# Revit family: Casual_Space_Division-Teknion-HNBCFG_Navigate_Fixed_Center_Screen_Glass-R2016
name_source: partatom
category: Furniture
revit_build: Autodesk Revit Architecture 2016 (Build: 20190507_1515(x64)
units: mm (PartAtom-declared; Revit-internal decimal feet)

## family parameters
Always vertical = Yes
Cut with Voids When Loaded = No
OmniClass Number = 23.40.20.00
OmniClass Title = General Furniture and Specialties
Room Calculation Point = No
Shared = Yes
Work Plane-Based = No

## types (2) — shared parameters
Assembly Code = E2020200
Manufacturer = Teknion
Manufacturer Fax = 416.661.4586
Part Number = HNBCFG
Product Documentation Link = https://www.teknion.com
Product Line = Height-Adjustable Bench
Product Page URL = https://www.teknion.com
Series = Height-Adjustable Bench
Sustainability Data = https://www.teknion.com
URL = www.teknion.com
Unit Weight URL = http://www.teknion.com
Warranty = http://www.teknion.com

## per-type parameters (varying)
| type | Description | Full Style | Inset Style | Model |
| 51" Height, Full Style | Navigate Fixed Center Screen – Glass, 51" Height, Full Style | Yes | No | HNBCFG51__F |
| 51" Height, Inset Style | Navigate Fixed Center Screen – Glass, 51" Height, Inset Style | No | Yes | HNBCFG51__I |

## geometry (parser evidence)
native form markers: Sweep x2
no freeform markers — native parametric forms only
